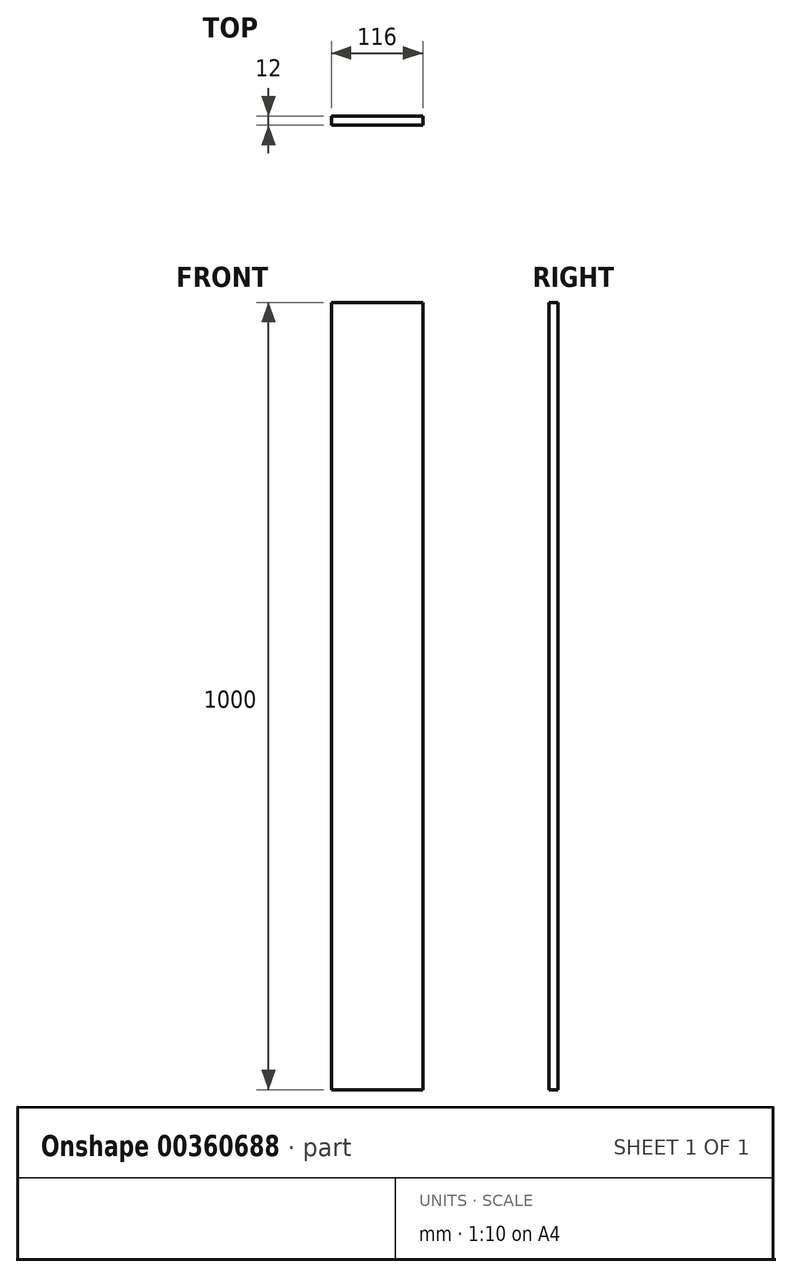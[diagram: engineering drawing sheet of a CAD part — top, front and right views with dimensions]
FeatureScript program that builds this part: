
annotation { "Feature Type Name" : "Feature", "Feature Type Description" : "" }
export const myFeature = defineFeature(function(context is Context, id is Id, definition is map)
    precondition{}
    {
        {
            var Q0;
            Q0=qCreatedBy(makeId("Front.planeOp"),FACE);
            var sketch = newSketch(context, id + "F0", { "sketchPlane" : qUnion([Q0])});
            skLineSegment(sketch, "E0.bottom", {"start": v(0, 0) * mm, "end": v(116, 0) * mm});
            skLineSegment(sketch, "E0.top", {"start": v(0, 1000) * mm, "end": v(116, 1000) * mm});
            skLineSegment(sketch, "E0.left", {"start": v(0, 0) * mm, "end": v(0, 1000) * mm});
            skLineSegment(sketch, "E0.right", {"start": v(116, 0) * mm, "end": v(116, 1000) * mm});
            skSolve(sketch);
        }
        {
            var Q0;
            Q0=makeQuery(id+"F0.imprint","IMPRINT",FACE,{"disambiguationData":[TD([[makeQuery(id+"F0.imprint","IMPRINT",EDGE,{"derivedFrom":sQuery(id+"F0.wireOp",EDGE,"E0.bottom")}),1.0]])]});
            extrude(context, id + "F1", {"entities" : qUnion([Q0]), "depth" : 12 * mm});
        }
    });
